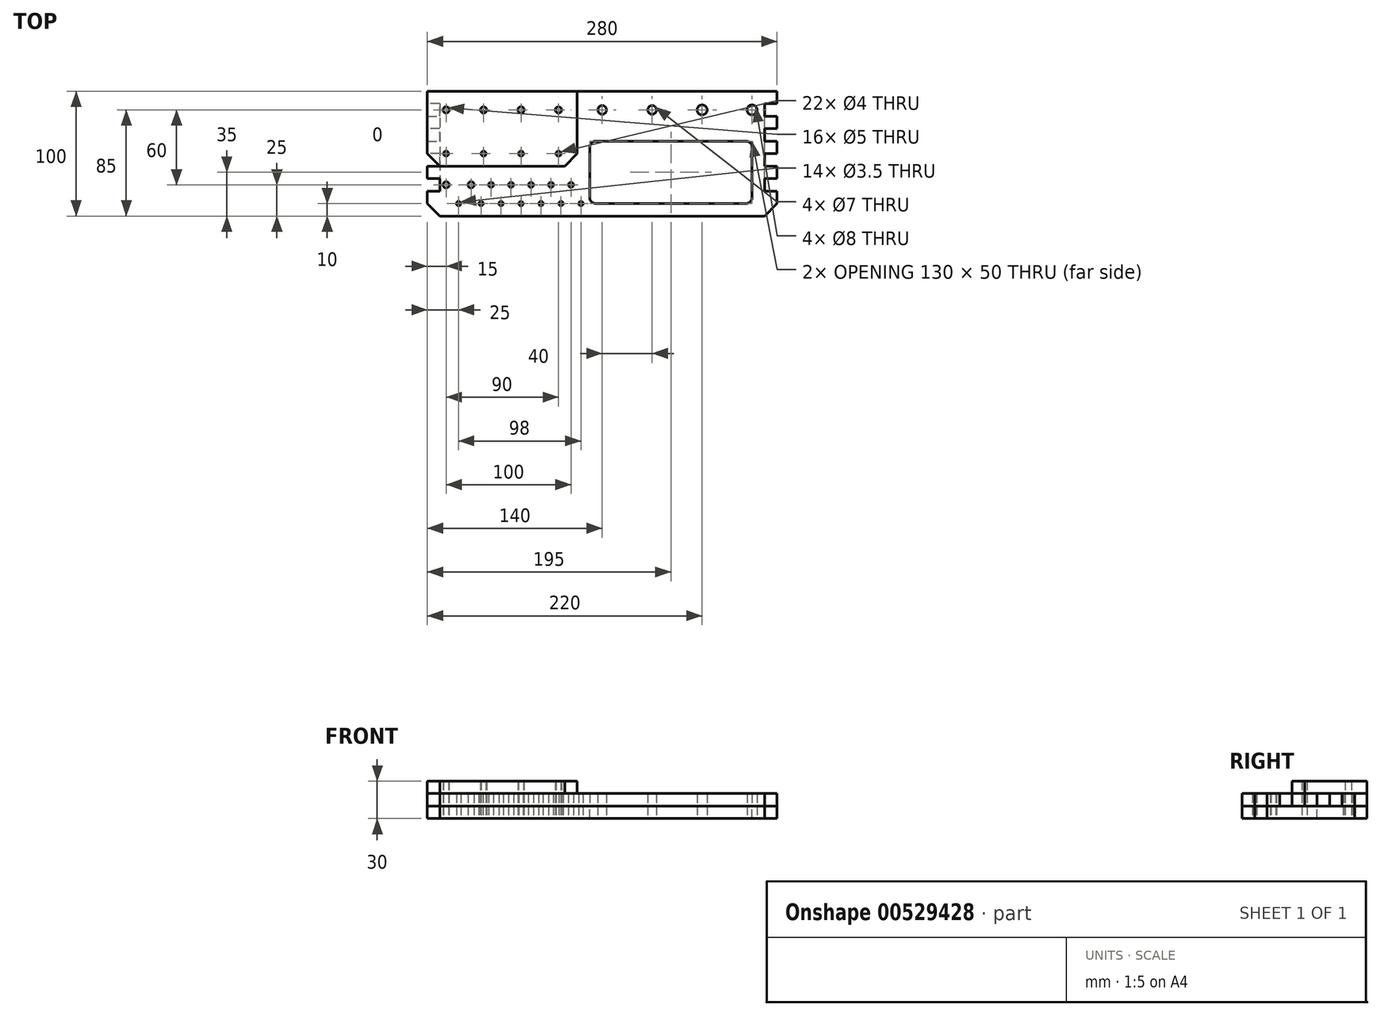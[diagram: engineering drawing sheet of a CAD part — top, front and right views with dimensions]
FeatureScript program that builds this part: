
annotation { "Feature Type Name" : "Feature", "Feature Type Description" : "" }
export const myFeature = defineFeature(function(context is Context, id is Id, definition is map)
    precondition{}
    {
        {
            var Q0;
            Q0=qCreatedBy(makeId("Top.planeOp"),FACE);
            var sketch = newSketch(context, id + "F0", { "sketchPlane" : qUnion([Q0])});
            skLineSegment(sketch, "E0.top", {"start": v(140, 50) * mm, "end": v(-140, 50) * mm});
            skPoint(sketch, "E0.middle", {"position": v(0, 0) * mm});
            skLineSegment(sketch, "E1", {"start": v(-140, -30) * mm, "end": v(-130, -30) * mm});
            skLineSegment(sketch, "E2", {"start": v(-130, -30) * mm, "end": v(-130, -20) * mm});
            skLineSegment(sketch, "E3", {"start": v(-130, -20) * mm, "end": v(-140, -20) * mm});
            skLineSegment(sketch, "E4", {"start": v(-140, -20) * mm, "end": v(-140, -10) * mm});
            skLineSegment(sketch, "E5", {"start": v(-140, -10) * mm, "end": v(-130, -10) * mm});
            skLineSegment(sketch, "E6", {"start": v(-130, -10) * mm, "end": v(-130, 0) * mm});
            skLineSegment(sketch, "E7", {"start": v(-130, 0) * mm, "end": v(-140, 0) * mm});
            skLineSegment(sketch, "E8", {"start": v(-140, 0) * mm, "end": v(-140, 10) * mm});
            skLineSegment(sketch, "E9", {"start": v(-140, 10) * mm, "end": v(-130, 10) * mm});
            skLineSegment(sketch, "E10", {"start": v(-130, 10) * mm, "end": v(-130, 20) * mm});
            skLineSegment(sketch, "E11", {"start": v(-130, 20) * mm, "end": v(-140, 20) * mm});
            skLineSegment(sketch, "E12", {"start": v(-140, 20) * mm, "end": v(-140, 30) * mm});
            skLineSegment(sketch, "E13", {"start": v(-140, 30) * mm, "end": v(-130, 30) * mm});
            skLineSegment(sketch, "E14", {"start": v(-130, 30) * mm, "end": v(-130, 40) * mm});
            skLineSegment(sketch, "E15", {"start": v(-130, 40) * mm, "end": v(-140, 40) * mm});
            skLineSegment(sketch, "E16", {"start": v(-140, 40) * mm, "end": v(-140, 50) * mm});
            skLineSegment(sketch, "E17", {"start": v(-130, -50) * mm, "end": v(-140, -40) * mm});
            skLineSegment(sketch, "E18", {"start": v(-140, -40) * mm, "end": v(-140, -30) * mm});
            skLineSegment(sketch, "E19.MirrorCS", {"start": v(130, -30) * mm, "end": v(130, -20) * mm});
            skLineSegment(sketch, "E20.MirrorCS", {"start": v(140, 20) * mm, "end": v(140, 30) * mm});
            skLineSegment(sketch, "E21.MirrorCS", {"start": v(130, 20) * mm, "end": v(140, 20) * mm});
            skLineSegment(sketch, "E22.MirrorCS", {"start": v(140, -30) * mm, "end": v(130, -30) * mm});
            skLineSegment(sketch, "E23.MirrorCS", {"start": v(130, 40) * mm, "end": v(140, 40) * mm});
            skLineSegment(sketch, "E24.MirrorCS", {"start": v(140, -10) * mm, "end": v(130, -10) * mm});
            skLineSegment(sketch, "E25.MirrorCS", {"start": v(140, -20) * mm, "end": v(140, -10) * mm});
            skLineSegment(sketch, "E26.MirrorCS", {"start": v(130, -20) * mm, "end": v(140, -20) * mm});
            skLineSegment(sketch, "E27.MirrorCS", {"start": v(130, 0) * mm, "end": v(140, 0) * mm});
            skLineSegment(sketch, "E28.MirrorCS", {"start": v(130, 30) * mm, "end": v(130, 40) * mm});
            skLineSegment(sketch, "E29.MirrorCS", {"start": v(140, 10) * mm, "end": v(130, 10) * mm});
            skLineSegment(sketch, "E30.MirrorCS", {"start": v(140, 0) * mm, "end": v(140, 10) * mm});
            skLineSegment(sketch, "E31.MirrorCS", {"start": v(140, -40) * mm, "end": v(140, -30) * mm});
            skLineSegment(sketch, "E32.MirrorCS", {"start": v(130, -10) * mm, "end": v(130, 0) * mm});
            skLineSegment(sketch, "E33.MirrorCS", {"start": v(130, 10) * mm, "end": v(130, 20) * mm});
            skLineSegment(sketch, "E34.MirrorCS", {"start": v(140, 30) * mm, "end": v(130, 30) * mm});
            skLineSegment(sketch, "E35.MirrorCS", {"start": v(130, -50) * mm, "end": v(140, -40) * mm});
            skLineSegment(sketch, "E36.MirrorCS", {"start": v(140, 40) * mm, "end": v(140, 50) * mm});
            skLineSegment(sketch, "E37", {"start": v(-130, -50) * mm, "end": v(130, -50) * mm});
            skLineSegment(sketch, "E38.bottom", {"start": v(120, -40) * mm, "end": v(-10, -40) * mm});
            skLineSegment(sketch, "E38.top", {"start": v(120, 10) * mm, "end": v(-10, 10) * mm});
            skLineSegment(sketch, "E38.left", {"start": v(120, -40) * mm, "end": v(120, 10) * mm});
            skLineSegment(sketch, "E38.right", {"start": v(-10, -40) * mm, "end": v(-10, 10) * mm});
            skSolve(sketch);
        }
        {
            var Q0;
            Q0=makeQuery(id+"F0.imprint","IMPRINT",FACE,{"disambiguationData":[TD([[makeQuery(id+"F0.imprint","IMPRINT",EDGE,{"derivedFrom":sQuery(id+"F0.wireOp",EDGE,"E0.top")}),1.0]])]});
            extrude(context, id + "F1", {"entities" : qUnion([Q0]), "depth" : 10 * mm, "offsetDistance" : 25 * mm});
        }
        {
            var Q0;
            Q0=makeQuery(id+"F1.opExtrude","SWEPT_EDGE",EDGE,{"disambiguationData":[OSD([sQuery(id+"F0.wireOp",EDGE,"E38.top"),sQuery(id+"F0.wireOp",EDGE,"E38.right")])]});
            var Q1;
            Q1=makeQuery(id+"F1.opExtrude","SWEPT_EDGE",EDGE,{"disambiguationData":[OSD([sQuery(id+"F0.wireOp",EDGE,"E38.top"),sQuery(id+"F0.wireOp",EDGE,"E38.left")])]});
            var Q2;
            Q2=makeQuery(id+"F1.opExtrude","SWEPT_EDGE",EDGE,{"disambiguationData":[OSD([sQuery(id+"F0.wireOp",EDGE,"E38.bottom"),sQuery(id+"F0.wireOp",EDGE,"E38.right")])]});
            var Q3;
            Q3=makeQuery(id+"F1.opExtrude","SWEPT_EDGE",EDGE,{"disambiguationData":[OSD([sQuery(id+"F0.wireOp",EDGE,"E38.bottom"),sQuery(id+"F0.wireOp",EDGE,"E38.left")])]});
            fillet(context, id + "F2", {"entities" : qUnion([Q0, Q1, Q2, Q3]), "radius" : 5 * mm, "tangentPropagation" : true, "allowEdgeOverflow" : false});
        }
        {
            var Q0;
            Q0=makeQuery(id+"F1.opExtrude","CAP_FACE",FACE,{"disambiguationData":[OSD([sQuery(id+"F0.wireOp",EDGE,"E0.top"),sQuery(id+"F0.wireOp",EDGE,"E1"),sQuery(id+"F0.wireOp",EDGE,"E2"),sQuery(id+"F0.wireOp",EDGE,"E3"),sQuery(id+"F0.wireOp",EDGE,"E4"),sQuery(id+"F0.wireOp",EDGE,"E5"),sQuery(id+"F0.wireOp",EDGE,"E6"),sQuery(id+"F0.wireOp",EDGE,"E7"),sQuery(id+"F0.wireOp",EDGE,"E8"),sQuery(id+"F0.wireOp",EDGE,"E9"),sQuery(id+"F0.wireOp",EDGE,"E10"),sQuery(id+"F0.wireOp",EDGE,"E11"),sQuery(id+"F0.wireOp",EDGE,"E12"),sQuery(id+"F0.wireOp",EDGE,"E13"),sQuery(id+"F0.wireOp",EDGE,"E14"),sQuery(id+"F0.wireOp",EDGE,"E15"),sQuery(id+"F0.wireOp",EDGE,"E16"),sQuery(id+"F0.wireOp",EDGE,"E17"),sQuery(id+"F0.wireOp",EDGE,"E18"),sQuery(id+"F0.wireOp",EDGE,"E19.MirrorCS"),sQuery(id+"F0.wireOp",EDGE,"E20.MirrorCS"),sQuery(id+"F0.wireOp",EDGE,"E21.MirrorCS"),sQuery(id+"F0.wireOp",EDGE,"E22.MirrorCS"),sQuery(id+"F0.wireOp",EDGE,"E23.MirrorCS"),sQuery(id+"F0.wireOp",EDGE,"E24.MirrorCS"),sQuery(id+"F0.wireOp",EDGE,"E25.MirrorCS"),sQuery(id+"F0.wireOp",EDGE,"E26.MirrorCS"),sQuery(id+"F0.wireOp",EDGE,"E27.MirrorCS"),sQuery(id+"F0.wireOp",EDGE,"E28.MirrorCS"),sQuery(id+"F0.wireOp",EDGE,"E29.MirrorCS"),sQuery(id+"F0.wireOp",EDGE,"E30.MirrorCS"),sQuery(id+"F0.wireOp",EDGE,"E31.MirrorCS"),sQuery(id+"F0.wireOp",EDGE,"E32.MirrorCS"),sQuery(id+"F0.wireOp",EDGE,"E33.MirrorCS"),sQuery(id+"F0.wireOp",EDGE,"E34.MirrorCS"),sQuery(id+"F0.wireOp",EDGE,"E35.MirrorCS"),sQuery(id+"F0.wireOp",EDGE,"E36.MirrorCS"),sQuery(id+"F0.wireOp",EDGE,"E37"),sQuery(id+"F0.wireOp",EDGE,"E38.bottom"),sQuery(id+"F0.wireOp",EDGE,"E38.top"),sQuery(id+"F0.wireOp",EDGE,"E38.left"),sQuery(id+"F0.wireOp",EDGE,"E38.right")])],"isStart":false});
            var sketch = newSketch(context, id + "F3", { "sketchPlane" : qUnion([Q0])});
            skLineSegment(sketch, "E39.bottom", {"start": v(-140, 50) * mm, "end": v(-20, 50) * mm});
            skLineSegment(sketch, "E39.top", {"start": v(-130, -10) * mm, "end": v(-30, -10) * mm});
            skLineSegment(sketch, "E39.left", {"start": v(-140, 50) * mm, "end": v(-140, 0) * mm});
            skLineSegment(sketch, "E39.right", {"start": v(-20, 50) * mm, "end": v(-20, 0) * mm});
            skLineSegment(sketch, "E40", {"start": v(-20, 0) * mm, "end": v(-30, -10) * mm});
            skLineSegment(sketch, "E41", {"start": v(-140, 0) * mm, "end": v(-130, -10) * mm});
            skSolve(sketch);
        }
        {
            var Q0;
            Q0 = qSketchRegion(id + "F3", true);
            extrude(context, id + "F4", {"entities" : qUnion([Q0]), "depth" : 10 * mm, "offsetDistance" : 25 * mm});
        }
        {
            var Q0;
            Q0=makeQuery(id+"F1.opExtrude","CAP_FACE",FACE,{"disambiguationData":[OSD([sQuery(id+"F0.wireOp",EDGE,"E0.top"),sQuery(id+"F0.wireOp",EDGE,"E1"),sQuery(id+"F0.wireOp",EDGE,"E2"),sQuery(id+"F0.wireOp",EDGE,"E3"),sQuery(id+"F0.wireOp",EDGE,"E4"),sQuery(id+"F0.wireOp",EDGE,"E5"),sQuery(id+"F0.wireOp",EDGE,"E6"),sQuery(id+"F0.wireOp",EDGE,"E7"),sQuery(id+"F0.wireOp",EDGE,"E8"),sQuery(id+"F0.wireOp",EDGE,"E9"),sQuery(id+"F0.wireOp",EDGE,"E10"),sQuery(id+"F0.wireOp",EDGE,"E11"),sQuery(id+"F0.wireOp",EDGE,"E12"),sQuery(id+"F0.wireOp",EDGE,"E13"),sQuery(id+"F0.wireOp",EDGE,"E14"),sQuery(id+"F0.wireOp",EDGE,"E15"),sQuery(id+"F0.wireOp",EDGE,"E16"),sQuery(id+"F0.wireOp",EDGE,"E17"),sQuery(id+"F0.wireOp",EDGE,"E18"),sQuery(id+"F0.wireOp",EDGE,"E19.MirrorCS"),sQuery(id+"F0.wireOp",EDGE,"E20.MirrorCS"),sQuery(id+"F0.wireOp",EDGE,"E21.MirrorCS"),sQuery(id+"F0.wireOp",EDGE,"E22.MirrorCS"),sQuery(id+"F0.wireOp",EDGE,"E23.MirrorCS"),sQuery(id+"F0.wireOp",EDGE,"E24.MirrorCS"),sQuery(id+"F0.wireOp",EDGE,"E25.MirrorCS"),sQuery(id+"F0.wireOp",EDGE,"E26.MirrorCS"),sQuery(id+"F0.wireOp",EDGE,"E27.MirrorCS"),sQuery(id+"F0.wireOp",EDGE,"E28.MirrorCS"),sQuery(id+"F0.wireOp",EDGE,"E29.MirrorCS"),sQuery(id+"F0.wireOp",EDGE,"E30.MirrorCS"),sQuery(id+"F0.wireOp",EDGE,"E31.MirrorCS"),sQuery(id+"F0.wireOp",EDGE,"E32.MirrorCS"),sQuery(id+"F0.wireOp",EDGE,"E33.MirrorCS"),sQuery(id+"F0.wireOp",EDGE,"E34.MirrorCS"),sQuery(id+"F0.wireOp",EDGE,"E35.MirrorCS"),sQuery(id+"F0.wireOp",EDGE,"E36.MirrorCS"),sQuery(id+"F0.wireOp",EDGE,"E37"),sQuery(id+"F0.wireOp",EDGE,"E38.bottom"),sQuery(id+"F0.wireOp",EDGE,"E38.top"),sQuery(id+"F0.wireOp",EDGE,"E38.left"),sQuery(id+"F0.wireOp",EDGE,"E38.right")])],"isStart":true});
            var sketch = newSketch(context, id + "F5", { "sketchPlane" : qUnion([Q0])});
            skLineSegment(sketch, "E42", {"start": v(-130, -40) * mm, "end": v(-130, 30) * mm});
            skLineSegment(sketch, "E43", {"start": v(-130, 30) * mm, "end": v(-140, 30) * mm});
            skLineSegment(sketch, "E44", {"start": v(-140, 30) * mm, "end": v(-140, 40) * mm});
            skLineSegment(sketch, "E45", {"start": v(-140, 40) * mm, "end": v(-130, 50) * mm});
            skLineSegment(sketch, "E46", {"start": v(-130, 50) * mm, "end": v(130, 50) * mm});
            skLineSegment(sketch, "E47", {"start": v(130, 50) * mm, "end": v(140, 40) * mm});
            skLineSegment(sketch, "E48", {"start": v(140, 40) * mm, "end": v(140, 30) * mm});
            skLineSegment(sketch, "E49", {"start": v(140, 30) * mm, "end": v(130, 30) * mm});
            skLineSegment(sketch, "E50", {"start": v(130, 30) * mm, "end": v(130, -40) * mm});
            skLineSegment(sketch, "E51", {"start": v(130, -50) * mm, "end": v(-130, -50) * mm});
            skLineSegment(sketch, "E52.0", {"start": v(115, 40) * mm, "end": v(-5, 40) * mm});
            skLineSegment(sketch, "E52.1", {"start": v(115, -10) * mm, "end": v(-5, -10) * mm});
            skLineSegment(sketch, "E52.2", {"start": v(120, 35) * mm, "end": v(120, -5) * mm});
            skLineSegment(sketch, "E52.3", {"start": v(-10, 35) * mm, "end": v(-10, -5) * mm});
            skArc(sketch, "E53", {"start": v(-10, 35) * mm, "mid": v(-8.54, 38.54) * mm, "end": v(-5, 40) * mm});
            skArc(sketch, "E54", {"start": v(115, 40) * mm, "mid": v(118.54, 38.54) * mm, "end": v(120, 35) * mm});
            skArc(sketch, "E55", {"start": v(120, -5) * mm, "mid": v(118.54, -8.54) * mm, "end": v(115, -10) * mm});
            skArc(sketch, "E56", {"start": v(-10, -5) * mm, "mid": v(-8.54, -8.54) * mm, "end": v(-5, -10) * mm});
            skLineSegment(sketch, "E57", {"start": v(-130, -40) * mm, "end": v(-140, -40) * mm});
            skLineSegment(sketch, "E58", {"start": v(-140, -40) * mm, "end": v(-140, -50) * mm});
            skLineSegment(sketch, "E59", {"start": v(-140, -50) * mm, "end": v(-130, -50) * mm});
            skLineSegment(sketch, "E60.MirrorCS", {"start": v(130, -40) * mm, "end": v(140, -40) * mm});
            skLineSegment(sketch, "E61.MirrorCS", {"start": v(140, -40) * mm, "end": v(140, -50) * mm});
            skLineSegment(sketch, "E62.MirrorCS", {"start": v(140, -50) * mm, "end": v(130, -50) * mm});
            skSolve(sketch);
        }
        {
            var Q0;
            Q0 = qSketchRegion(id + "F5", true);
            extrude(context, id + "F6", {"entities" : qUnion([Q0]), "depth" : 10 * mm, "offsetDistance" : 25 * mm});
        }
        {
            var Q0;
            Q0=makeQuery(id+"F1.opExtrude","CAP_FACE",FACE,{"disambiguationData":[OSD([sQuery(id+"F0.wireOp",EDGE,"E0.top"),sQuery(id+"F0.wireOp",EDGE,"E1"),sQuery(id+"F0.wireOp",EDGE,"E2"),sQuery(id+"F0.wireOp",EDGE,"E3"),sQuery(id+"F0.wireOp",EDGE,"E4"),sQuery(id+"F0.wireOp",EDGE,"E5"),sQuery(id+"F0.wireOp",EDGE,"E6"),sQuery(id+"F0.wireOp",EDGE,"E7"),sQuery(id+"F0.wireOp",EDGE,"E8"),sQuery(id+"F0.wireOp",EDGE,"E9"),sQuery(id+"F0.wireOp",EDGE,"E10"),sQuery(id+"F0.wireOp",EDGE,"E11"),sQuery(id+"F0.wireOp",EDGE,"E12"),sQuery(id+"F0.wireOp",EDGE,"E13"),sQuery(id+"F0.wireOp",EDGE,"E14"),sQuery(id+"F0.wireOp",EDGE,"E15"),sQuery(id+"F0.wireOp",EDGE,"E16"),sQuery(id+"F0.wireOp",EDGE,"E17"),sQuery(id+"F0.wireOp",EDGE,"E18"),sQuery(id+"F0.wireOp",EDGE,"E19.MirrorCS"),sQuery(id+"F0.wireOp",EDGE,"E20.MirrorCS"),sQuery(id+"F0.wireOp",EDGE,"E21.MirrorCS"),sQuery(id+"F0.wireOp",EDGE,"E22.MirrorCS"),sQuery(id+"F0.wireOp",EDGE,"E23.MirrorCS"),sQuery(id+"F0.wireOp",EDGE,"E24.MirrorCS"),sQuery(id+"F0.wireOp",EDGE,"E25.MirrorCS"),sQuery(id+"F0.wireOp",EDGE,"E26.MirrorCS"),sQuery(id+"F0.wireOp",EDGE,"E27.MirrorCS"),sQuery(id+"F0.wireOp",EDGE,"E28.MirrorCS"),sQuery(id+"F0.wireOp",EDGE,"E29.MirrorCS"),sQuery(id+"F0.wireOp",EDGE,"E30.MirrorCS"),sQuery(id+"F0.wireOp",EDGE,"E31.MirrorCS"),sQuery(id+"F0.wireOp",EDGE,"E32.MirrorCS"),sQuery(id+"F0.wireOp",EDGE,"E33.MirrorCS"),sQuery(id+"F0.wireOp",EDGE,"E34.MirrorCS"),sQuery(id+"F0.wireOp",EDGE,"E35.MirrorCS"),sQuery(id+"F0.wireOp",EDGE,"E36.MirrorCS"),sQuery(id+"F0.wireOp",EDGE,"E37"),sQuery(id+"F0.wireOp",EDGE,"E38.bottom"),sQuery(id+"F0.wireOp",EDGE,"E38.top"),sQuery(id+"F0.wireOp",EDGE,"E38.left"),sQuery(id+"F0.wireOp",EDGE,"E38.right")])],"isStart":false});
            var sketch = newSketch(context, id + "F7", { "sketchPlane" : qUnion([Q0])});
            skCircle(sketch, "E63", {"center": v(120, 35) * mm, "radius": 4 * mm});
            skCircle(sketch, "E64", {"center": v(80, 35) * mm, "radius": 4 * mm});
            skCircle(sketch, "E65", {"center": v(40, 35) * mm, "radius": 3.5 * mm});
            skCircle(sketch, "E66", {"center": v(0, 35) * mm, "radius": 3.5 * mm});
            skCircle(sketch, "E67", {"center": v(-35, 35) * mm, "radius": 2.5 * mm});
            skCircle(sketch, "E68", {"center": v(-65, 35) * mm, "radius": 2.5 * mm});
            skCircle(sketch, "E69", {"center": v(-95, 35) * mm, "radius": 2.5 * mm});
            skCircle(sketch, "E70", {"center": v(-125, 35) * mm, "radius": 2.5 * mm});
            skCircle(sketch, "E71", {"center": v(-35, 0) * mm, "radius": 2 * mm});
            skCircle(sketch, "E72", {"center": v(-65, 0) * mm, "radius": 2 * mm});
            skCircle(sketch, "E73", {"center": v(-95, 0) * mm, "radius": 2 * mm});
            skCircle(sketch, "E74", {"center": v(-125, 0) * mm, "radius": 2 * mm});
            skCircle(sketch, "E75", {"center": v(-125, -25) * mm, "radius": 2.5 * mm});
            skCircle(sketch, "E76", {"center": v(-105, -25) * mm, "radius": 2.5 * mm});
            skCircle(sketch, "E77", {"center": v(-89, -25) * mm, "radius": 2 * mm});
            skCircle(sketch, "E78", {"center": v(-73, -25) * mm, "radius": 2 * mm});
            skCircle(sketch, "E79", {"center": v(-57, -25) * mm, "radius": 2 * mm});
            skCircle(sketch, "E80", {"center": v(-41, -25) * mm, "radius": 2 * mm});
            skCircle(sketch, "E81", {"center": v(-25, -25) * mm, "radius": 2 * mm});
            skCircle(sketch, "E82", {"center": v(-115, -40) * mm, "radius": 1.75 * mm});
            skCircle(sketch, "E83", {"center": v(-97, -40) * mm, "radius": 1.75 * mm});
            skCircle(sketch, "E84", {"center": v(-81, -40) * mm, "radius": 1.75 * mm});
            skCircle(sketch, "E85", {"center": v(-65, -40) * mm, "radius": 1.75 * mm});
            skCircle(sketch, "E86", {"center": v(-49, -40) * mm, "radius": 1.75 * mm});
            skCircle(sketch, "E87", {"center": v(-33, -40) * mm, "radius": 1.75 * mm});
            skCircle(sketch, "E88", {"center": v(-17, -40) * mm, "radius": 1.75 * mm});
            skSolve(sketch);
        }
        {
            var Q0;
            Q0=makeQuery(id+"F7.imprint","IMPRINT",FACE,{"disambiguationData":[TD([[makeQuery(id+"F7.imprint","IMPRINT",EDGE,{"derivedFrom":sQuery(id+"F7.wireOp",EDGE,"E66")}),1.0]])]});
            var Q1;
            Q1=makeQuery(id+"F7.imprint","IMPRINT",FACE,{"disambiguationData":[TD([[makeQuery(id+"F7.imprint","IMPRINT",EDGE,{"derivedFrom":sQuery(id+"F7.wireOp",EDGE,"E65")}),1.0]])]});
            var Q2;
            Q2=makeQuery(id+"F7.imprint","IMPRINT",FACE,{"disambiguationData":[TD([[makeQuery(id+"F7.imprint","IMPRINT",EDGE,{"derivedFrom":sQuery(id+"F7.wireOp",EDGE,"E64")}),1.0]])]});
            var Q3;
            Q3=makeQuery(id+"F7.imprint","IMPRINT",FACE,{"disambiguationData":[TD([[makeQuery(id+"F7.imprint","IMPRINT",EDGE,{"derivedFrom":sQuery(id+"F7.wireOp",EDGE,"E63")}),1.0]])]});
            var Q4;
            Q4=makeQuery(id+"F7.imprint","IMPRINT",FACE,{"disambiguationData":[TD([[makeQuery(id+"F7.imprint","IMPRINT",EDGE,{"derivedFrom":sQuery(id+"F7.wireOp",EDGE,"E67")}),1.0]])]});
            var Q5;
            Q5=makeQuery(id+"F7.imprint","IMPRINT",FACE,{"disambiguationData":[TD([[makeQuery(id+"F7.imprint","IMPRINT",EDGE,{"derivedFrom":sQuery(id+"F7.wireOp",EDGE,"E68")}),1.0]])]});
            var Q6;
            Q6=makeQuery(id+"F7.imprint","IMPRINT",FACE,{"disambiguationData":[TD([[makeQuery(id+"F7.imprint","IMPRINT",EDGE,{"derivedFrom":sQuery(id+"F7.wireOp",EDGE,"E69")}),1.0]])]});
            var Q7;
            Q7=makeQuery(id+"F7.imprint","IMPRINT",FACE,{"disambiguationData":[TD([[makeQuery(id+"F7.imprint","IMPRINT",EDGE,{"derivedFrom":sQuery(id+"F7.wireOp",EDGE,"E70")}),1.0]])]});
            var Q8;
            Q8=makeQuery(id+"F7.imprint","IMPRINT",FACE,{"disambiguationData":[TD([[makeQuery(id+"F7.imprint","IMPRINT",EDGE,{"derivedFrom":sQuery(id+"F7.wireOp",EDGE,"E71")}),1.0]])]});
            var Q9;
            Q9=makeQuery(id+"F7.imprint","IMPRINT",FACE,{"disambiguationData":[TD([[makeQuery(id+"F7.imprint","IMPRINT",EDGE,{"derivedFrom":sQuery(id+"F7.wireOp",EDGE,"E72")}),1.0]])]});
            var Q10;
            Q10=makeQuery(id+"F7.imprint","IMPRINT",FACE,{"disambiguationData":[TD([[makeQuery(id+"F7.imprint","IMPRINT",EDGE,{"derivedFrom":sQuery(id+"F7.wireOp",EDGE,"E73")}),1.0]])]});
            var Q11;
            Q11=makeQuery(id+"F7.imprint","IMPRINT",FACE,{"disambiguationData":[TD([[makeQuery(id+"F7.imprint","IMPRINT",EDGE,{"derivedFrom":sQuery(id+"F7.wireOp",EDGE,"E74")}),1.0]])]});
            var Q12;
            Q12=makeQuery(id+"F7.imprint","IMPRINT",FACE,{"disambiguationData":[TD([[makeQuery(id+"F7.imprint","IMPRINT",EDGE,{"derivedFrom":sQuery(id+"F7.wireOp",EDGE,"E75")}),1.0]])]});
            var Q13;
            Q13=makeQuery(id+"F7.imprint","IMPRINT",FACE,{"disambiguationData":[TD([[makeQuery(id+"F7.imprint","IMPRINT",EDGE,{"derivedFrom":sQuery(id+"F7.wireOp",EDGE,"E76")}),1.0]])]});
            var Q14;
            Q14=makeQuery(id+"F7.imprint","IMPRINT",FACE,{"disambiguationData":[TD([[makeQuery(id+"F7.imprint","IMPRINT",EDGE,{"derivedFrom":sQuery(id+"F7.wireOp",EDGE,"E77")}),1.0]])]});
            var Q15;
            Q15=makeQuery(id+"F7.imprint","IMPRINT",FACE,{"disambiguationData":[TD([[makeQuery(id+"F7.imprint","IMPRINT",EDGE,{"derivedFrom":sQuery(id+"F7.wireOp",EDGE,"E78")}),1.0]])]});
            var Q16;
            Q16=makeQuery(id+"F7.imprint","IMPRINT",FACE,{"disambiguationData":[TD([[makeQuery(id+"F7.imprint","IMPRINT",EDGE,{"derivedFrom":sQuery(id+"F7.wireOp",EDGE,"E79")}),1.0]])]});
            var Q17;
            Q17=makeQuery(id+"F7.imprint","IMPRINT",FACE,{"disambiguationData":[TD([[makeQuery(id+"F7.imprint","IMPRINT",EDGE,{"derivedFrom":sQuery(id+"F7.wireOp",EDGE,"E80")}),1.0]])]});
            var Q18;
            Q18=makeQuery(id+"F7.imprint","IMPRINT",FACE,{"disambiguationData":[TD([[makeQuery(id+"F7.imprint","IMPRINT",EDGE,{"derivedFrom":sQuery(id+"F7.wireOp",EDGE,"E81")}),1.0]])]});
            var Q19;
            Q19=makeQuery(id+"F7.imprint","IMPRINT",FACE,{"disambiguationData":[TD([[makeQuery(id+"F7.imprint","IMPRINT",EDGE,{"derivedFrom":sQuery(id+"F7.wireOp",EDGE,"E82")}),1.0]])]});
            var Q20;
            Q20=makeQuery(id+"F7.imprint","IMPRINT",FACE,{"disambiguationData":[TD([[makeQuery(id+"F7.imprint","IMPRINT",EDGE,{"derivedFrom":sQuery(id+"F7.wireOp",EDGE,"E83")}),1.0]])]});
            var Q21;
            Q21=makeQuery(id+"F7.imprint","IMPRINT",FACE,{"disambiguationData":[TD([[makeQuery(id+"F7.imprint","IMPRINT",EDGE,{"derivedFrom":sQuery(id+"F7.wireOp",EDGE,"E84")}),1.0]])]});
            var Q22;
            Q22=makeQuery(id+"F7.imprint","IMPRINT",FACE,{"disambiguationData":[TD([[makeQuery(id+"F7.imprint","IMPRINT",EDGE,{"derivedFrom":sQuery(id+"F7.wireOp",EDGE,"E85")}),1.0]])]});
            var Q23;
            Q23=makeQuery(id+"F7.imprint","IMPRINT",FACE,{"disambiguationData":[TD([[makeQuery(id+"F7.imprint","IMPRINT",EDGE,{"derivedFrom":sQuery(id+"F7.wireOp",EDGE,"E86")}),1.0]])]});
            var Q24;
            Q24=makeQuery(id+"F7.imprint","IMPRINT",FACE,{"disambiguationData":[TD([[makeQuery(id+"F7.imprint","IMPRINT",EDGE,{"derivedFrom":sQuery(id+"F7.wireOp",EDGE,"E87")}),1.0]])]});
            var Q25;
            Q25=makeQuery(id+"F7.imprint","IMPRINT",FACE,{"disambiguationData":[TD([[makeQuery(id+"F7.imprint","IMPRINT",EDGE,{"derivedFrom":sQuery(id+"F7.wireOp",EDGE,"E88")}),1.0]])]});
            extrude(context, id + "F8", {"entities" : qUnion([Q0, Q1, Q2, Q3, Q4, Q5, Q6, Q7, Q8, Q9, Q10, Q11, Q12, Q13, Q14, Q15, Q16, Q17, Q18, Q19, Q20, Q21, Q22, Q23, Q24, Q25]), "operationType" : NewBodyOperationType.REMOVE, "endBound" : BoundingType.SYMMETRIC, "depth" : 50 * mm, "offsetDistance" : 25 * mm});
        }
    });
